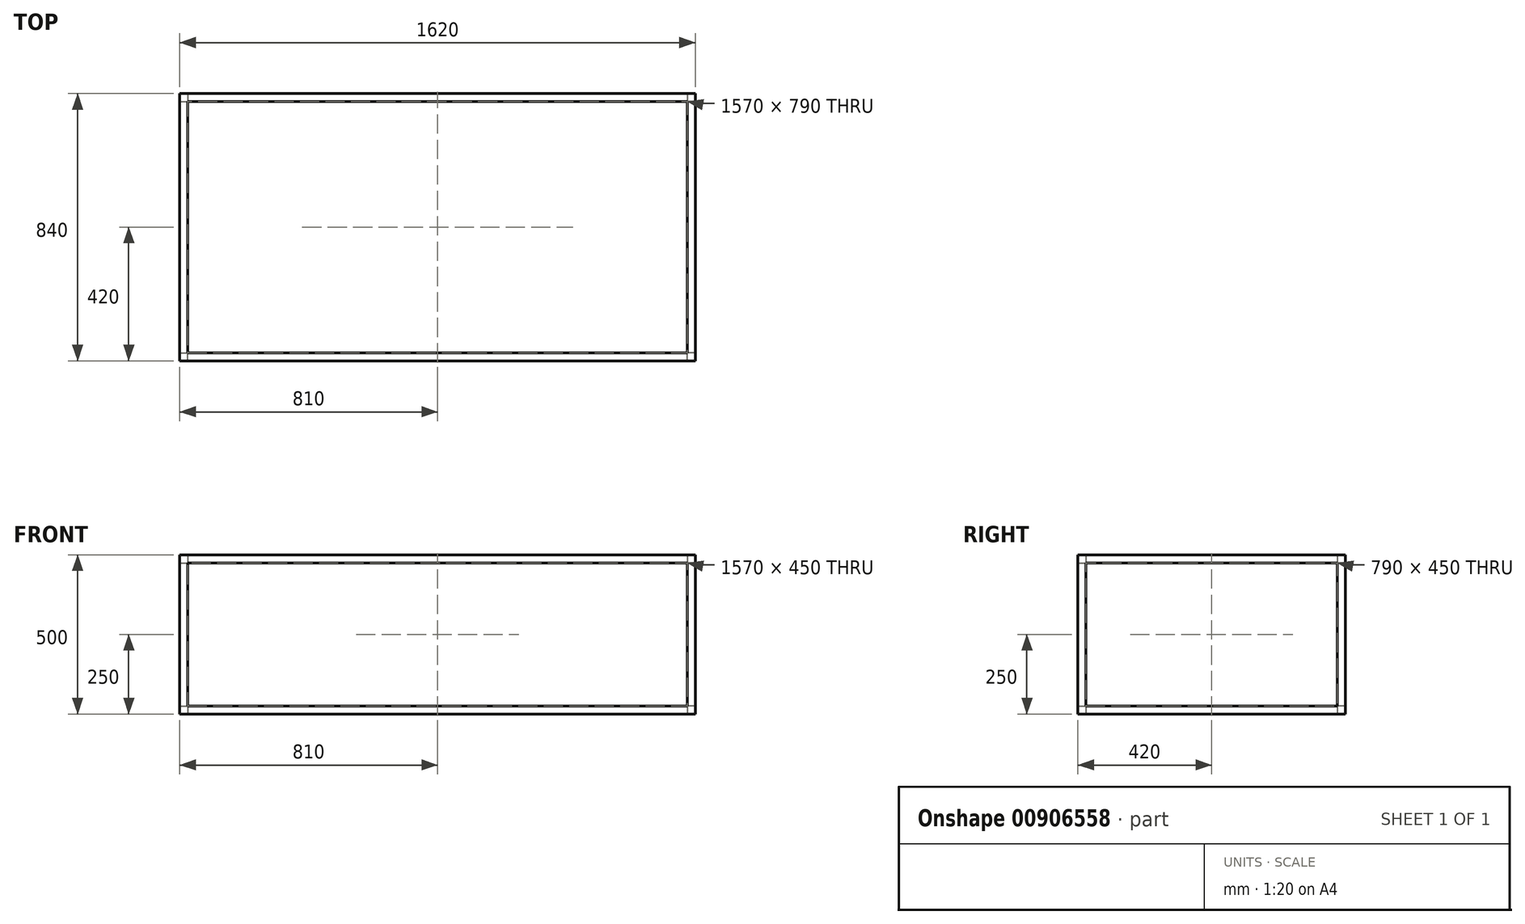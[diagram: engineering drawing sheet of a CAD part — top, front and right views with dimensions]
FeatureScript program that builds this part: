
annotation { "Feature Type Name" : "Feature", "Feature Type Description" : "" }
export const myFeature = defineFeature(function(context is Context, id is Id, definition is map)
    precondition{}
    {
        {
            var Q0;
            Q0=qCreatedBy(makeId("Top.planeOp"),FACE);
            var sketch = newSketch(context, id + "F0", { "sketchPlane" : qUnion([Q0])});
            skLineSegment(sketch, "E0.bottom", {"start": v(0, 0) * mm, "end": v(-1620, 0) * mm});
            skLineSegment(sketch, "E0.top", {"start": v(0, 840) * mm, "end": v(-1620, 840) * mm});
            skLineSegment(sketch, "E0.left", {"start": v(0, 0) * mm, "end": v(0, 840) * mm});
            skLineSegment(sketch, "E0.right", {"start": v(-1620, 0) * mm, "end": v(-1620, 840) * mm});
            skLineSegment(sketch, "E1.top", {"start": v(-1595, 815) * mm, "end": v(-810, 815) * mm});
            skLineSegment(sketch, "E1.left", {"start": v(-1595, 420) * mm, "end": v(-1595, 815) * mm});
            skLineSegment(sketch, "E2.top", {"start": v(-1595, 25) * mm, "end": v(-810, 25) * mm});
            skLineSegment(sketch, "E2.left", {"start": v(-1595, 420) * mm, "end": v(-1595, 25) * mm});
            skLineSegment(sketch, "E3.bottom", {"start": v(-810, 25) * mm, "end": v(-25, 25) * mm});
            skLineSegment(sketch, "E3.right", {"start": v(-25, 25) * mm, "end": v(-25, 420) * mm});
            skLineSegment(sketch, "E4.bottom", {"start": v(-810, 815) * mm, "end": v(-25, 815) * mm});
            skLineSegment(sketch, "E4.right", {"start": v(-25, 815) * mm, "end": v(-25, 420) * mm});
            skLineSegment(sketch, "E5", {"start": v(-1595, 815) * mm, "end": v(-1620, 840) * mm});
            skLineSegment(sketch, "E6", {"start": v(-25, 815) * mm, "end": v(0, 840) * mm});
            skLineSegment(sketch, "E7", {"start": v(-1595, 25) * mm, "end": v(-1620, 0) * mm});
            skLineSegment(sketch, "E8", {"start": v(-25, 25) * mm, "end": v(0, 0) * mm});
            skSolve(sketch);
        }
        {
            var Q0;
            Q0=qSketchRegion(id+"F0",true);
            extrude(context, id + "F1", {"entities" : qUnion([Q0]), "depth" : 25 * mm, "offsetDistance" : 25 * mm});
        }
        {
            var Q0;
            Q0=makeQuery(id+"F1.opExtrude","CAP_FACE",FACE,{"disambiguationData":[OSD([sQuery(id+"F0.wireOp",EDGE,"E0.bottom"),sQuery(id+"F0.wireOp",EDGE,"E0.top"),sQuery(id+"F0.wireOp",EDGE,"E0.left"),sQuery(id+"F0.wireOp",EDGE,"E0.right"),sQuery(id+"F0.wireOp",EDGE,"E1.top"),sQuery(id+"F0.wireOp",EDGE,"E1.left"),sQuery(id+"F0.wireOp",EDGE,"E2.top"),sQuery(id+"F0.wireOp",EDGE,"E2.left"),sQuery(id+"F0.wireOp",EDGE,"E3.bottom"),sQuery(id+"F0.wireOp",EDGE,"E3.right"),sQuery(id+"F0.wireOp",EDGE,"E4.bottom"),sQuery(id+"F0.wireOp",EDGE,"E4.right")])],"isStart":false});
            var sketch = newSketch(context, id + "F2", { "sketchPlane" : qUnion([Q0])});
            skLineSegment(sketch, "E9.bottom", {"start": v(-1620, 0) * mm, "end": v(-1595, 0) * mm});
            skLineSegment(sketch, "E9.top", {"start": v(-1620, 25) * mm, "end": v(-1595, 25) * mm});
            skLineSegment(sketch, "E9.left", {"start": v(-1620, 0) * mm, "end": v(-1620, 25) * mm});
            skLineSegment(sketch, "E9.right", {"start": v(-1595, 0) * mm, "end": v(-1595, 25) * mm});
            skLineSegment(sketch, "E10.bottom", {"start": v(-1620, 840) * mm, "end": v(-1595, 840) * mm});
            skLineSegment(sketch, "E10.top", {"start": v(-1620, 815) * mm, "end": v(-1595, 815) * mm});
            skLineSegment(sketch, "E10.left", {"start": v(-1620, 840) * mm, "end": v(-1620, 815) * mm});
            skLineSegment(sketch, "E10.right", {"start": v(-1595, 840) * mm, "end": v(-1595, 815) * mm});
            skLineSegment(sketch, "E11.bottom", {"start": v(0, 840) * mm, "end": v(-25, 840) * mm});
            skLineSegment(sketch, "E11.top", {"start": v(0, 815) * mm, "end": v(-25, 815) * mm});
            skLineSegment(sketch, "E11.left", {"start": v(0, 840) * mm, "end": v(0, 815) * mm});
            skLineSegment(sketch, "E11.right", {"start": v(-25, 840) * mm, "end": v(-25, 815) * mm});
            skLineSegment(sketch, "E12.bottom", {"start": v(0, 0) * mm, "end": v(-25, 0) * mm});
            skLineSegment(sketch, "E12.top", {"start": v(0, 25) * mm, "end": v(-25, 25) * mm});
            skLineSegment(sketch, "E12.left", {"start": v(0, 0) * mm, "end": v(0, 25) * mm});
            skLineSegment(sketch, "E12.right", {"start": v(-25, 0) * mm, "end": v(-25, 25) * mm});
            skSolve(sketch);
        }
        {
            var Q0;
            Q0=makeQuery(id+"F2.imprint","IMPRINT",FACE,{"disambiguationData":[TD([[makeQuery(id+"F2.imprint","IMPRINT",EDGE,{"derivedFrom":sQuery(id+"F2.wireOp",EDGE,"E9.bottom")}),-1.0]])]});
            var Q1;
            Q1=makeQuery(id+"F2.imprint","IMPRINT",FACE,{"disambiguationData":[TD([[makeQuery(id+"F2.imprint","IMPRINT",EDGE,{"derivedFrom":sQuery(id+"F2.wireOp",EDGE,"E10.bottom")}),1.0]])]});
            var Q2;
            Q2=makeQuery(id+"F2.imprint","IMPRINT",FACE,{"disambiguationData":[TD([[makeQuery(id+"F2.imprint","IMPRINT",EDGE,{"derivedFrom":sQuery(id+"F2.wireOp",EDGE,"E12.bottom")}),-1.0]])]});
            var Q3;
            Q3=makeQuery(id+"F2.imprint","IMPRINT",FACE,{"disambiguationData":[TD([[makeQuery(id+"F2.imprint","IMPRINT",EDGE,{"derivedFrom":sQuery(id+"F2.wireOp",EDGE,"E11.bottom")}),1.0]])]});
            extrude(context, id + "F3", {"entities" : qUnion([Q0, Q1, Q2, Q3]), "operationType" : NewBodyOperationType.ADD, "depth" : 450 * mm, "offsetDistance" : 25 * mm});
        }
        {
            var Q0;
            Q0=makeQuery(id+"F3.opExtrude","CAP_FACE",FACE,{"disambiguationData":[OSD([sQuery(id+"F2.wireOp",EDGE,"E11.bottom"),sQuery(id+"F2.wireOp",EDGE,"E11.top"),sQuery(id+"F2.wireOp",EDGE,"E11.left"),sQuery(id+"F2.wireOp",EDGE,"E11.right")])],"isStart":false});
            var sketch = newSketch(context, id + "F4", { "sketchPlane" : qUnion([Q0])});
            skLineSegment(sketch, "E13.bottom", {"start": v(0, 840) * mm, "end": v(-1620, 840) * mm});
            skLineSegment(sketch, "E13.top", {"start": v(0, 0) * mm, "end": v(-1620, 0) * mm});
            skLineSegment(sketch, "E13.left", {"start": v(0, 840) * mm, "end": v(0, 0) * mm});
            skLineSegment(sketch, "E13.right", {"start": v(-1620, 840) * mm, "end": v(-1620, 0) * mm});
            skLineSegment(sketch, "E14.top", {"start": v(-1595, 815) * mm, "end": v(-810, 815) * mm});
            skLineSegment(sketch, "E14.left", {"start": v(-1595, 420) * mm, "end": v(-1595, 815) * mm});
            skLineSegment(sketch, "E15.bottom", {"start": v(-810, 25) * mm, "end": v(-25, 25) * mm});
            skLineSegment(sketch, "E15.right", {"start": v(-25, 25) * mm, "end": v(-25, 420) * mm});
            skLineSegment(sketch, "E16.bottom", {"start": v(-810, 25) * mm, "end": v(-1595, 25) * mm});
            skLineSegment(sketch, "E16.right", {"start": v(-1595, 25) * mm, "end": v(-1595, 420) * mm});
            skLineSegment(sketch, "E17.top", {"start": v(-25, 815) * mm, "end": v(-810, 815) * mm});
            skLineSegment(sketch, "E17.left", {"start": v(-25, 420) * mm, "end": v(-25, 815) * mm});
            skLineSegment(sketch, "E18", {"start": v(0, 0) * mm, "end": v(-25, 25) * mm});
            skLineSegment(sketch, "E19", {"start": v(0, 840) * mm, "end": v(-25, 815) * mm});
            skLineSegment(sketch, "E20", {"start": v(-1620, 840) * mm, "end": v(-1595, 815) * mm});
            skLineSegment(sketch, "E21", {"start": v(-1620, 0) * mm, "end": v(-1595, 25) * mm});
            skSolve(sketch);
        }
        {
            var Q0;
            Q0=qSketchRegion(id+"F4",true);
            extrude(context, id + "F5", {"entities" : qUnion([Q0]), "operationType" : NewBodyOperationType.ADD, "depth" : 25 * mm, "offsetDistance" : 25 * mm});
        }
    });
